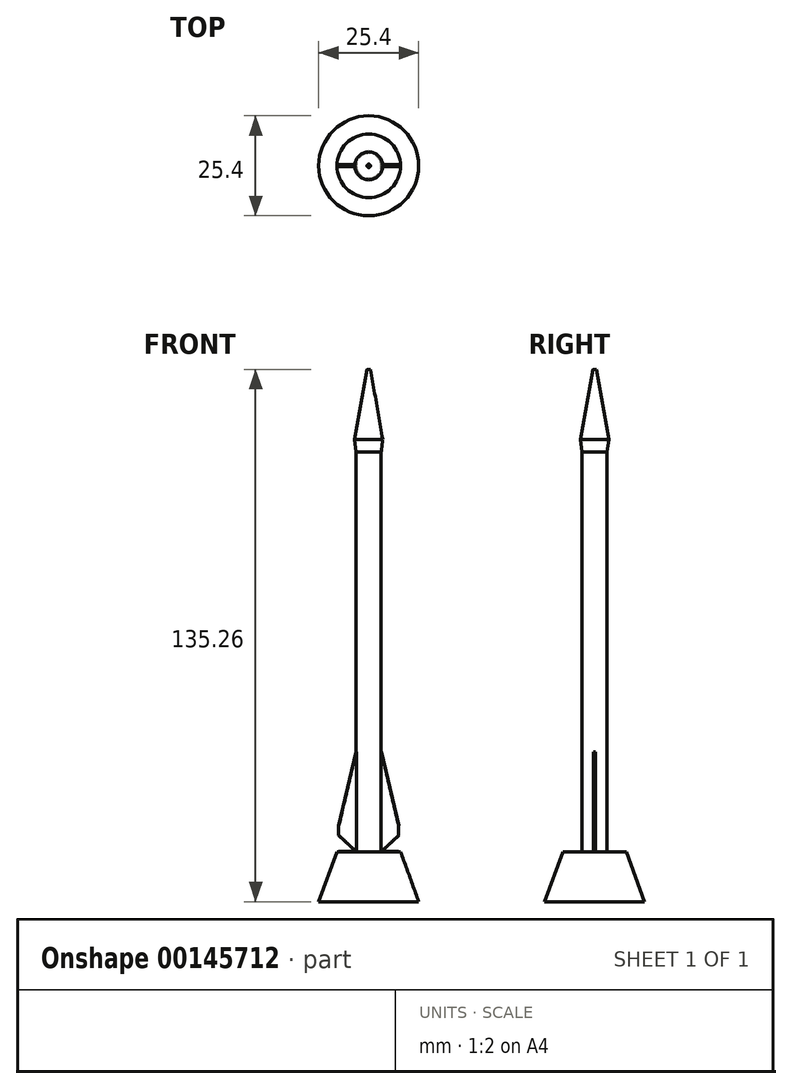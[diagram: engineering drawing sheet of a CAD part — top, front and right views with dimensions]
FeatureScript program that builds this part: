
annotation { "Feature Type Name" : "Feature", "Feature Type Description" : "" }
export const myFeature = defineFeature(function(context is Context, id is Id, definition is map)
    precondition{}
    {
        {
            var Q0;
            Q0=qCreatedBy(makeId("Top.planeOp"),FACE);
            var sketch = newSketch(context, id + "F0", { "sketchPlane" : qUnion([Q0])});
            skCircle(sketch, "E0", {"center": v(0, 0) * mm, "radius": 12.7 * mm});
            skSolve(sketch);
        }
        {
            var Q0;
            Q0 = qSketchRegion(id + "F0", true);
            extrude(context, id + "F1", {"entities" : qUnion([Q0]), "depth" : 12.7 * mm, "hasDraft" : true, "draftAngle" : 20 * degree, "draftPullDirection" : true});
        }
        {
            var Q0;
            Q0=makeQuery(id+"F1.opExtrude","CAP_FACE",FACE,{"disambiguationData":[OSD([sQuery(id+"F0.wireOp",EDGE,"E0")])],"isStart":false});
            var sketch = newSketch(context, id + "F2", { "sketchPlane" : qUnion([Q0])});
            skCircle(sketch, "E1", {"center": v(0, 0) * mm, "radius": 3.17 * mm});
            skSolve(sketch);
        }
        {
            var Q0;
            Q0 = qSketchRegion(id + "F2", true);
            extrude(context, id + "F3", {"entities" : qUnion([Q0]), "operationType" : NewBodyOperationType.ADD, "depth" : 101.6 * mm});
        }
        {
            var Q0;
            Q0=makeQuery(id+"F3.opExtrude","CAP_FACE",FACE,{"disambiguationData":[OSD([sQuery(id+"F2.wireOp",EDGE,"E1")])],"isStart":false});
            var sketch = newSketch(context, id + "F4", { "sketchPlane" : qUnion([Q0])});
            skCircle(sketch, "E2", {"center": v(0, 0) * mm, "radius": 3.17 * mm});
            skSolve(sketch);
        }
        {
            var Q0;
            Q0 = qSketchRegion(id + "F4", true);
            extrude(context, id + "F5", {"entities" : qUnion([Q0]), "operationType" : NewBodyOperationType.ADD, "depth" : 3.17 * mm, "hasDraft" : true, "draftAngle" : 7 * degree});
        }
        {
            var Q0;
            Q0=makeQuery(id+"F5.opExtrude","CAP_FACE",FACE,{"disambiguationData":[OSD([sQuery(id+"F4.wireOp",EDGE,"E2")])],"isStart":false});
            var sketch = newSketch(context, id + "F6", { "sketchPlane" : qUnion([Q0])});
            skCircle(sketch, "E3", {"center": v(0, 0) * mm, "radius": 3.56 * mm});
            skSolve(sketch);
        }
        {
            var Q0;
            Q0 = qSketchRegion(id + "F6", true);
            extrude(context, id + "F7", {"entities" : qUnion([Q0]), "operationType" : NewBodyOperationType.ADD, "depth" : 17.78 * mm, "hasDraft" : true, "draftAngle" : 10 * degree, "draftPullDirection" : true});
        }
        {
            var Q0;
            Q0=qCreatedBy(makeId("Top.planeOp"),FACE);
            var sketch = newSketch(context, id + "F8", { "sketchPlane" : qUnion([Q0])});
            skLineSegment(sketch, "E4.bottom", {"start": v(7.62, 0.25) * mm, "end": v(-7.62, 0.25) * mm});
            skLineSegment(sketch, "E4.top", {"start": v(7.62, -0.25) * mm, "end": v(-7.62, -0.25) * mm});
            skLineSegment(sketch, "E4.left", {"start": v(7.62, 0.25) * mm, "end": v(7.62, -0.25) * mm});
            skLineSegment(sketch, "E4.right", {"start": v(-7.62, 0.25) * mm, "end": v(-7.62, -0.25) * mm});
            skPoint(sketch, "E4.middle", {"position": v(0, 0) * mm});
            skSolve(sketch);
        }
        {
            var Q0;
            Q0 = qSketchRegion(id + "F8", true);
            extrude(context, id + "F9", {"entities" : qUnion([Q0]), "operationType" : NewBodyOperationType.ADD, "depth" : 38.1 * mm});
        }
        {
            var Q0;
            Q0=qCreatedBy(makeId("Front.planeOp"),FACE);
            var sketch = newSketch(context, id + "F10", { "sketchPlane" : qUnion([Q0])});
            skLineSegment(sketch, "E5", {"start": v(-3.18, 38.33) * mm, "end": v(-8.08, 17.26) * mm});
            skLineSegment(sketch, "E6", {"start": v(-8.08, 17.26) * mm, "end": v(-3.18, 12.72) * mm});
            skLineSegment(sketch, "E7", {"start": v(-3.18, 12.72) * mm, "end": v(-11.77, 12.72) * mm});
            skLineSegment(sketch, "E8", {"start": v(-11.77, 12.72) * mm, "end": v(-8.69, 39.84) * mm});
            skLineSegment(sketch, "E9", {"start": v(-8.69, 39.84) * mm, "end": v(-3.18, 38.33) * mm});
            skSolve(sketch);
        }
        {
            var Q0;
            Q0=qCreatedBy(makeId("Front.planeOp"),FACE);
            var sketch = newSketch(context, id + "F11", { "sketchPlane" : qUnion([Q0])});
            skLineSegment(sketch, "E10", {"start": v(0, 0) * mm, "end": v(0, -9.85) * mm, "construction": true});
            skSolve(sketch);
        }
        {
            var Q0;
            Q0 = qSketchRegion(id + "F10", true);
            var Q1;
            Q1=sQuery(id+"F11.wireOp",EDGE,"E10");
            revolve(context, id + "F12", {"operationType" : NewBodyOperationType.REMOVE, "entities" : qUnion([Q0]), "axis" : qUnion([Q1]), "revolveType" : RevolveType.FULL, "oppositeDirection" : true});
        }
    });
